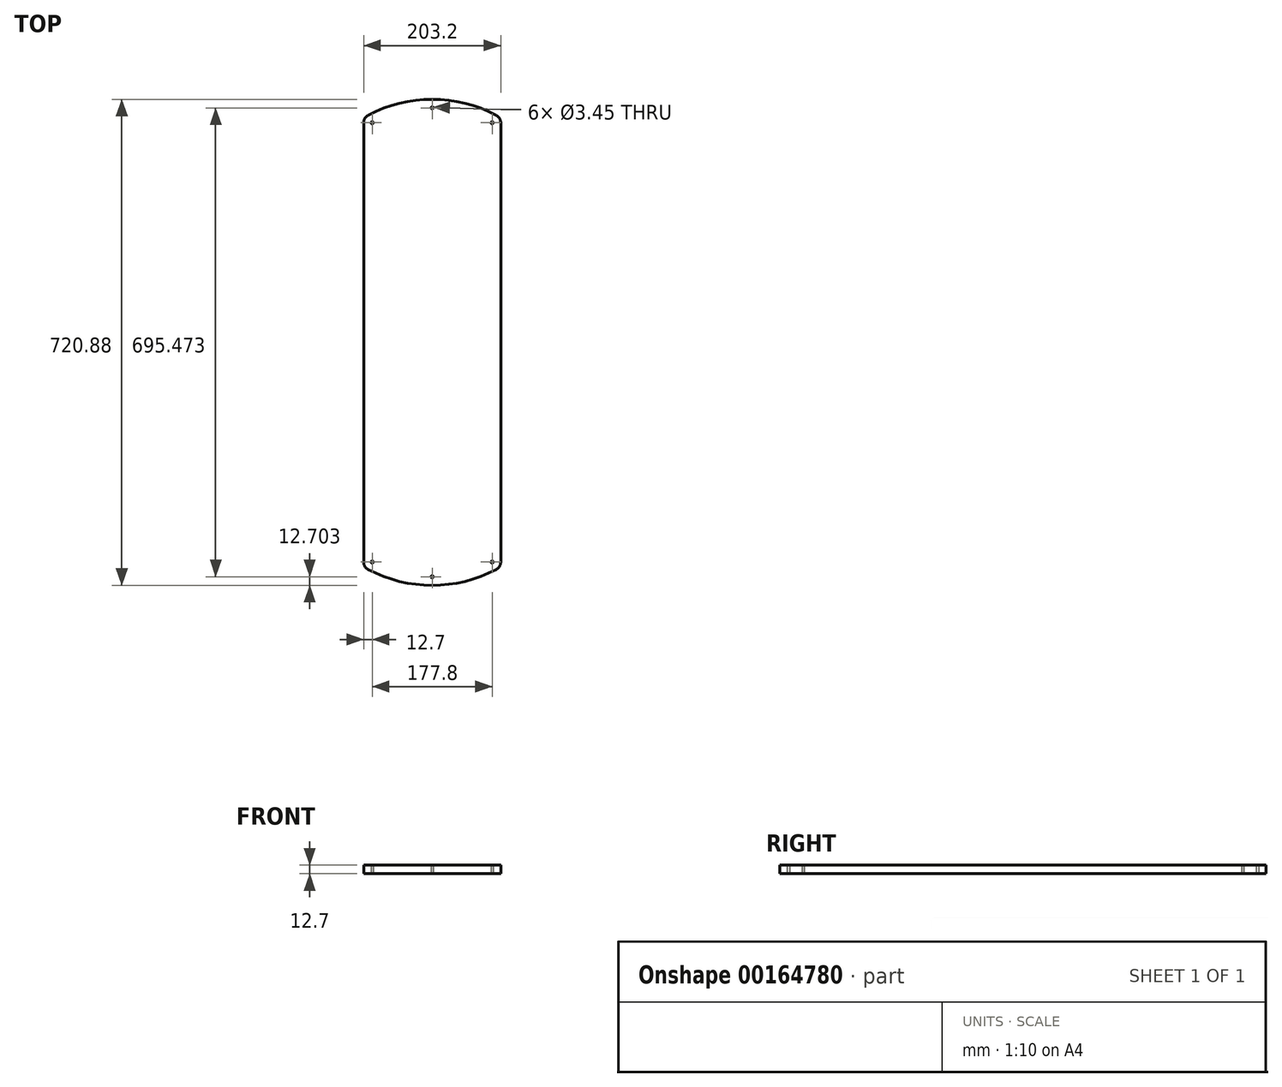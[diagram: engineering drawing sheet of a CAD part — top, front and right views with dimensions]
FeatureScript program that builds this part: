
annotation { "Feature Type Name" : "Feature", "Feature Type Description" : "" }
export const myFeature = defineFeature(function(context is Context, id is Id, definition is map)
    precondition{}
    {
        {
            var Q0;
            Q0=qCreatedBy(makeId("Top.planeOp"),FACE);
            var sketch = newSketch(context, id + "F0", { "sketchPlane" : qUnion([Q0])});
            skLineSegment(sketch, "E0.bottom", {"start": v(101.6, 325.72) * mm, "end": v(-101.6, 325.72) * mm, "construction": true});
            skLineSegment(sketch, "E0.top", {"start": v(101.6, -325.72) * mm, "end": v(-101.6, -325.72) * mm, "construction": true});
            skLineSegment(sketch, "E0.left", {"start": v(101.6, 325.72) * mm, "end": v(101.6, -325.72) * mm});
            skLineSegment(sketch, "E0.right", {"start": v(-101.6, 325.72) * mm, "end": v(-101.6, -325.72) * mm});
            skPoint(sketch, "E0.middle", {"position": v(0, 0) * mm});
            skArc(sketch, "E1", {"start": v(94.83, 336.95) * mm, "mid": v(0, 360.44) * mm, "end": v(-94.83, 336.95) * mm});
            skLineSegment(sketch, "E2", {"start": v(0, 325.72) * mm, "end": v(0, 157.24) * mm, "construction": true});
            skLineSegment(sketch, "E3", {"start": v(0, -157.24) * mm, "end": v(0, -325.72) * mm, "construction": true});
            skLineSegment(sketch, "E4", {"start": v(0, 157.24) * mm, "end": v(44.45, 241.48) * mm, "construction": true});
            skLineSegment(sketch, "E5", {"start": v(-44.45, 241.48) * mm, "end": v(0, 157.24) * mm, "construction": true});
            skLineSegment(sketch, "E6", {"start": v(0, 325.72) * mm, "end": v(0, 347.74) * mm, "construction": true});
            skCircle(sketch, "E7", {"center": v(0, 347.74) * mm, "radius": 12.7 * mm, "construction": true});
            skLineSegment(sketch, "E8", {"start": v(0, 241.48) * mm, "end": v(-44.45, 241.48) * mm, "construction": true});
            skLineSegment(sketch, "E9", {"start": v(0, 241.48) * mm, "end": v(44.45, 241.48) * mm, "construction": true});
            skLineSegment(sketch, "E10", {"start": v(-44.45, 241.48) * mm, "end": v(-88.9, 325.72) * mm, "construction": true});
            skLineSegment(sketch, "E11", {"start": v(44.45, 241.48) * mm, "end": v(88.9, 325.72) * mm, "construction": true});
            skCircle(sketch, "E12", {"center": v(-88.9, 325.72) * mm, "radius": 1.73 * mm});
            skCircle(sketch, "E13", {"center": v(88.9, 325.72) * mm, "radius": 1.73 * mm});
            skCircle(sketch, "E14", {"center": v(0, 347.74) * mm, "radius": 1.73 * mm});
            skArc(sketch, "E15", {"start": v(94.83, -336.95) * mm, "mid": v(99.78, -332.28) * mm, "end": v(101.6, -325.72) * mm});
            skArc(sketch, "E16", {"start": v(-101.6, -325.72) * mm, "mid": v(-99.78, -332.28) * mm, "end": v(-94.83, -336.95) * mm});
            skArc(sketch, "E17", {"start": v(-94.83, -336.95) * mm, "mid": v(0, -360.44) * mm, "end": v(94.83, -336.95) * mm});
            skArc(sketch, "E18", {"start": v(-94.83, 336.95) * mm, "mid": v(-99.78, 332.28) * mm, "end": v(-101.6, 325.72) * mm});
            skArc(sketch, "E19", {"start": v(101.6, 325.72) * mm, "mid": v(99.78, 332.28) * mm, "end": v(94.83, 336.95) * mm});
            skCircle(sketch, "E20", {"center": v(88.9, -325.72) * mm, "radius": 1.73 * mm});
            skCircle(sketch, "E21", {"center": v(-88.9, -325.72) * mm, "radius": 1.73 * mm});
            skLineSegment(sketch, "E22", {"start": v(0, -325.72) * mm, "end": v(0, -347.74) * mm, "construction": true});
            skCircle(sketch, "E23", {"center": v(0, -347.74) * mm, "radius": 12.7 * mm, "construction": true});
            skCircle(sketch, "E24", {"center": v(0, -347.74) * mm, "radius": 1.73 * mm});
            skSolve(sketch);
        }
        {
            var Q0;
            Q0=qSketchRegion(id+"F0",true);
            extrude(context, id + "F1", {"entities" : qUnion([Q0]), "depth" : 12.7 * mm});
        }
    });
